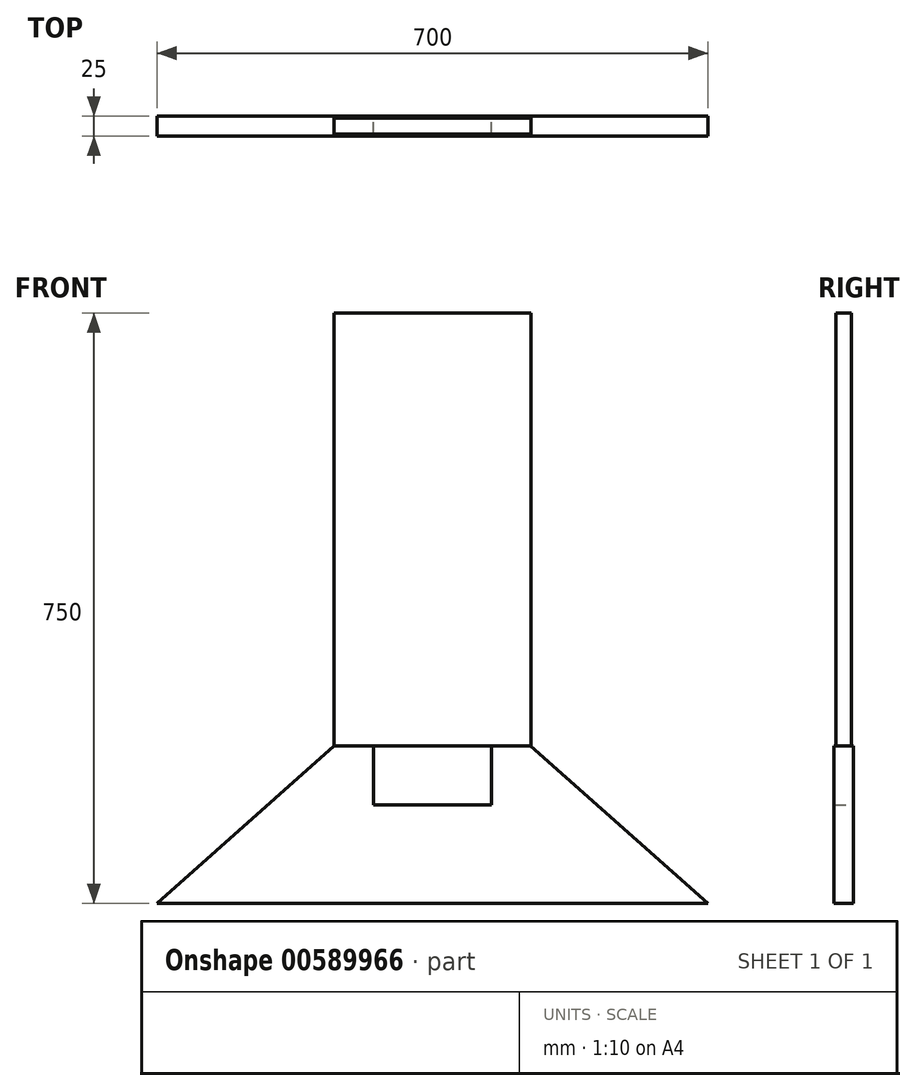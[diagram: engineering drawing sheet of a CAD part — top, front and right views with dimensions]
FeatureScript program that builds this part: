
annotation { "Feature Type Name" : "Feature", "Feature Type Description" : "" }
export const myFeature = defineFeature(function(context is Context, id is Id, definition is map)
    precondition{}
    {
        {
            var Q0;
            Q0=qCreatedBy(makeId("Top.planeOp"),FACE);
            var sketch = newSketch(context, id + "F0", { "sketchPlane" : qUnion([Q0])});
            skLineSegment(sketch, "E0.bottom", {"start": v(125, 10) * mm, "end": v(-125, 10) * mm});
            skLineSegment(sketch, "E0.top", {"start": v(125, -10) * mm, "end": v(-125, -10) * mm});
            skLineSegment(sketch, "E0.left", {"start": v(125, 10) * mm, "end": v(125, -10) * mm});
            skLineSegment(sketch, "E0.right", {"start": v(-125, 10) * mm, "end": v(-125, -10) * mm});
            skPoint(sketch, "E0.middle", {"position": v(0, 0) * mm});
            skSolve(sketch);
        }
        {
            var Q0;
            Q0=makeQuery(id+"F0.imprint","IMPRINT",FACE,{"disambiguationData":[TD([[makeQuery(id+"F0.imprint","IMPRINT",EDGE,{"derivedFrom":sQuery(id+"F0.wireOp",EDGE,"E0.bottom")}),1.0]])]});
            extrude(context, id + "F1", {"entities" : qUnion([Q0]), "depth" : 550 * mm, "offsetDistance" : 25 * mm});
        }
        {
            var Q0;
            Q0=qCreatedBy(makeId("Front.planeOp"),FACE);
            var sketch = newSketch(context, id + "F2", { "sketchPlane" : qUnion([Q0])});
            skLineSegment(sketch, "E1.bottom", {"start": v(75, -75) * mm, "end": v(-75, -75) * mm});
            skLineSegment(sketch, "E1.left", {"start": v(75, -75) * mm, "end": v(75, 0) * mm});
            skLineSegment(sketch, "E1.right", {"start": v(-75, -75) * mm, "end": v(-75, 0) * mm});
            skPoint(sketch, "E1.middle", {"position": v(0, 0) * mm});
            skLineSegment(sketch, "E2.bottom", {"start": v(350, -200) * mm, "end": v(-350, -200) * mm});
            skLineSegment(sketch, "E3", {"start": v(-350, -200) * mm, "end": v(-125.05, 0) * mm});
            skPoint(sketch, "E3.endSnap0", {"position": v(-75, 0) * mm});
            skLineSegment(sketch, "E4", {"start": v(-125.05, 0) * mm, "end": v(-75, 0) * mm});
            skLineSegment(sketch, "E5", {"start": v(350, -200) * mm, "end": v(124.92, 0) * mm});
            skLineSegment(sketch, "E6", {"start": v(124.92, 0) * mm, "end": v(75, 0) * mm});
            skPoint(sketch, "E2.left.end.orphan", {"position": v(350, 200) * mm});
            skPoint(sketch, "E2.right.end.orphan", {"position": v(-350, 200) * mm});
            skPoint(sketch, "E1.top.start.orphan", {"position": v(75, 75) * mm});
            skPoint(sketch, "E7.orphan", {"position": v(-75, 75) * mm});
            skSolve(sketch);
        }
        {
            var Q0;
            Q0=makeQuery(id+"F2.imprint","IMPRINT",FACE,{"disambiguationData":[TD([[makeQuery(id+"F2.imprint","IMPRINT",EDGE,{"derivedFrom":sQuery(id+"F2.wireOp",EDGE,"E1.bottom")}),1.0]])]});
            extrude(context, id + "F3", {"entities" : qUnion([Q0]), "operationType" : NewBodyOperationType.ADD, "endBound" : BoundingType.SYMMETRIC, "depth" : 25 * mm, "offsetDistance" : 25 * mm});
        }
    });
